# Revit family: 6kt.Schraube DIN EN ISO 4017, fvz, M12x40
name_source: partatom
category: HLS-Bauteile
units: mm (PartAtom-declared; Revit-internal decimal feet)

## family parameters
Arbeitsebenenbasiert = Ja
Beim Laden mit Abzugskörper schneiden = Nein
Bemaßung runder Anschluss = Durchmesser verwenden
Beschriftungsausrichtung beibehalten = Nein
Gemeinsam genutzt = Ja
Immer vertikal = Nein
Raumberechnungspunkt = Nein
Teiletyp = Normal

## types (1)
- M12x40, fvz
    Artikelnummer = 3206606/fvz
    EAN = 4250928457127
    Fabrikat = MEFA
    Festigkeitsklasse = 8.8
    Form Kopf = Sechskantkopf
    Gewicht = 0.05 kg
    Gewicht pro Bauteil = 0.05 kg
    Gewinde = M12
    H = 8 mm  [stored 0.0262467 ft]
    Kurztext1 = Sechskantschraube EN ISO 4017
    Kurztext2 = M12 x 40 mm fvz FK 8.8
    L = 40 mm  [stored 0.131234 ft]
    Länge = 40 mm  [stored 0.131234 ft]
    Material = Stahl
    Mengeneinheit = St
    R = 10 mm  [stored 0.0328084 ft]
    Schlüsselweite = 19
    Vorgabe-Ansicht = 1219 mm
    d2 = 5 mm  [stored 0.0164042 ft]
    vpe = 100

note: [stored X ft] marks values corroborated as IEEE doubles in the binary element streams (Revit-internal decimal feet)
